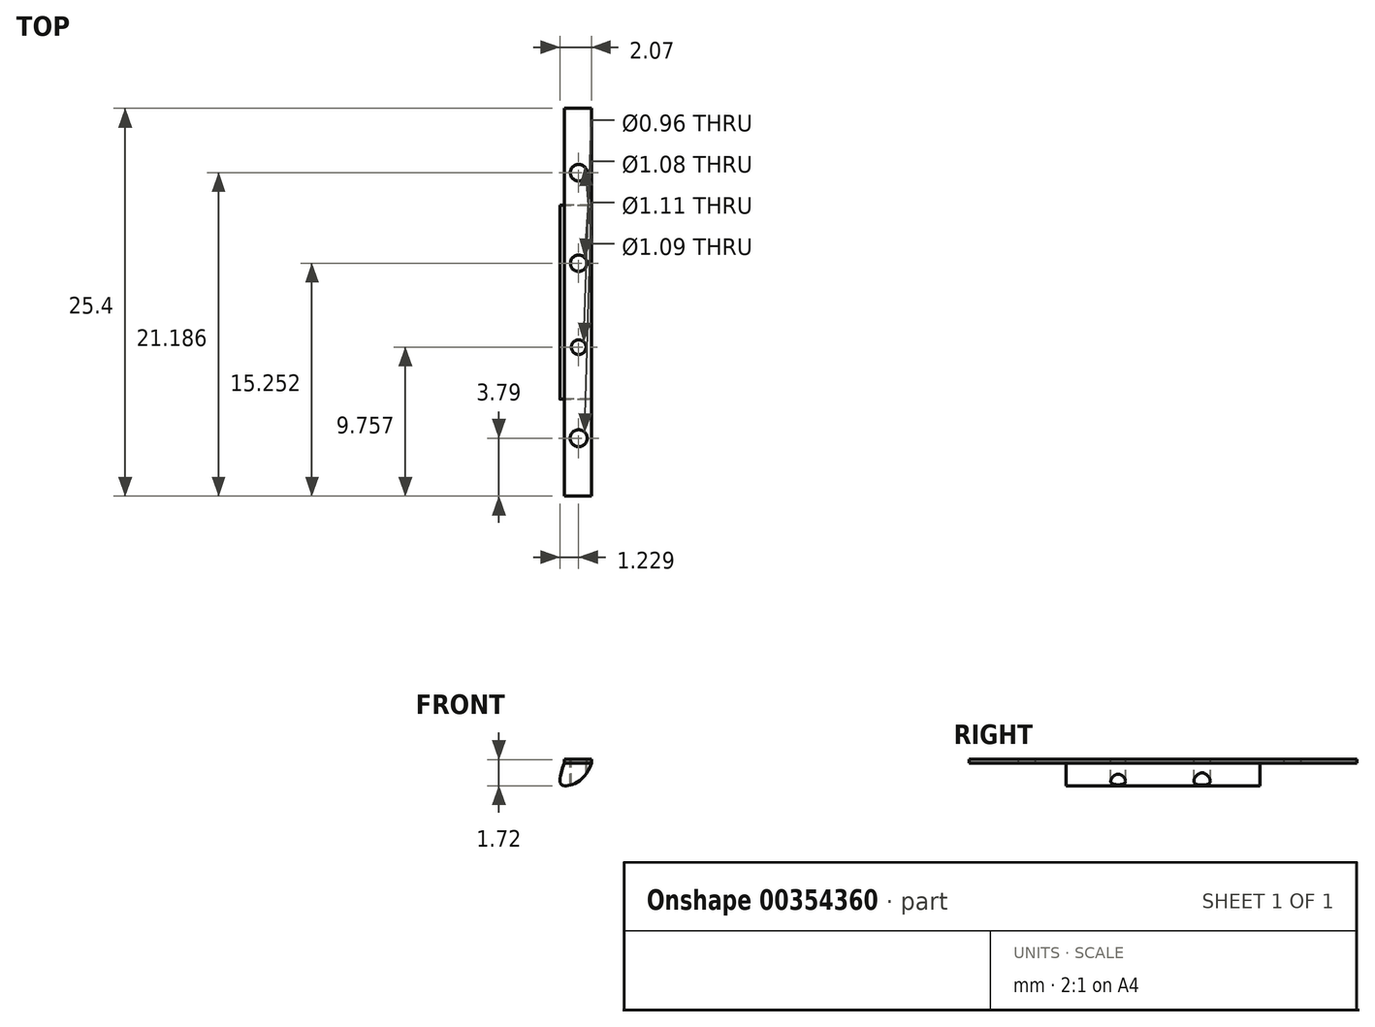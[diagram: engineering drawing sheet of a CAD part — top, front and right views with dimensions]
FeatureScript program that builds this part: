
annotation { "Feature Type Name" : "Feature", "Feature Type Description" : "" }
export const myFeature = defineFeature(function(context is Context, id is Id, definition is map)
    precondition{}
    {
        {
            var Q0;
            Q0=qCreatedBy(makeId("Front.planeOp"),FACE);
            var sketch = newSketch(context, id + "F0", { "sketchPlane" : qUnion([Q0])});
            skLineSegment(sketch, "E0", {"start": v(-34.8, 33.52) * mm, "end": v(-33.03, 33.52) * mm});
            skFitSpline(sketch, "E1", {"points": [v(-34.8, 33.52) * mm, v(-34.76, 32.05) * mm, v(-33.03, 33.52) * mm], "startDerivative": vector(-3.03, -7.7) * mm, "endDerivative": vector(1.94, 5.94) * mm});
            skLineSegment(sketch, "E2", {"start": v(-33.03, 33.52) * mm, "end": v(-33.03, 33.77) * mm});
            skLineSegment(sketch, "E3", {"start": v(-33.03, 33.77) * mm, "end": v(-34.8, 33.77) * mm});
            skLineSegment(sketch, "E4", {"start": v(-34.8, 33.77) * mm, "end": v(-34.8, 33.52) * mm});
            skSolve(sketch);
        }
        {
            var Q0;
            Q0 = qSketchRegion(id + "F0", true);
            extrude(context, id + "F1", {"entities" : qUnion([Q0]), "endBound" : BoundingType.SYMMETRIC, "depth" : 12.7 * mm});
        }
        {
            var Q0;
            Q0=qCreatedBy(makeId("Top.planeOp"),FACE);
            cPlane(context, id + "F2", {"entities" : qUnion([Q0]), "cplaneType" : CPlaneType.OFFSET, "offset" : 33.78 * mm, "width" : 152.4 * mm, "height" : 152.4 * mm});
        }
        {
            var Q0;
            Q0=qCreatedBy(id+"F2.planeOp",FACE);
            var sketch = newSketch(context, id + "F3", { "sketchPlane" : qUnion([Q0])});
            skCircle(sketch, "E5", {"center": v(-33.87, -2.94) * mm, "radius": 0.48 * mm});
            skCircle(sketch, "E6", {"center": v(-33.87, 2.55) * mm, "radius": 0.54 * mm});
            skCircle(sketch, "E7", {"center": v(-33.87, 8.49) * mm, "radius": 0.54 * mm});
            skCircle(sketch, "E8", {"center": v(-33.87, -8.9) * mm, "radius": 0.56 * mm});
            skSolve(sketch);
        }
        {
            var Q0;
            Q0=makeQuery(id+"F0.imprint","IMPRINT",FACE,{"disambiguationData":[TD([[makeQuery(id+"F0.imprint","IMPRINT",EDGE,{"derivedFrom":sQuery(id+"F0.wireOp",EDGE,"E0")}),1.0]])]});
            extrude(context, id + "F4", {"entities" : qUnion([Q0]), "operationType" : NewBodyOperationType.ADD, "endBound" : BoundingType.SYMMETRIC, "depth" : 25.4 * mm});
        }
        {
            var Q0;
            Q0=makeQuery(id+"F3.imprint","IMPRINT",FACE,{"disambiguationData":[TD([[makeQuery(id+"F3.imprint","IMPRINT",EDGE,{"derivedFrom":sQuery(id+"F3.wireOp",EDGE,"E6")}),1.0]])]});
            var Q1;
            Q1=makeQuery(id+"F3.imprint","IMPRINT",FACE,{"disambiguationData":[TD([[makeQuery(id+"F3.imprint","IMPRINT",EDGE,{"derivedFrom":sQuery(id+"F3.wireOp",EDGE,"E5")}),1.0]])]});
            extrude(context, id + "F5", {"entities" : qUnion([Q0, Q1]), "operationType" : NewBodyOperationType.REMOVE, "oppositeDirection" : true, "depth" : 12.7 * mm});
        }
        {
            var Q0;
            Q0=makeQuery(id+"F3.imprint","IMPRINT",FACE,{"disambiguationData":[TD([[makeQuery(id+"F3.imprint","IMPRINT",EDGE,{"derivedFrom":sQuery(id+"F3.wireOp",EDGE,"E8")}),1.0]])]});
            var Q1;
            Q1=makeQuery(id+"F3.imprint","IMPRINT",FACE,{"disambiguationData":[TD([[makeQuery(id+"F3.imprint","IMPRINT",EDGE,{"derivedFrom":sQuery(id+"F3.wireOp",EDGE,"E7")}),1.0]])]});
            extrude(context, id + "F6", {"entities" : qUnion([Q0, Q1]), "operationType" : NewBodyOperationType.REMOVE, "oppositeDirection" : true, "depth" : 12.7 * mm});
        }
    });
